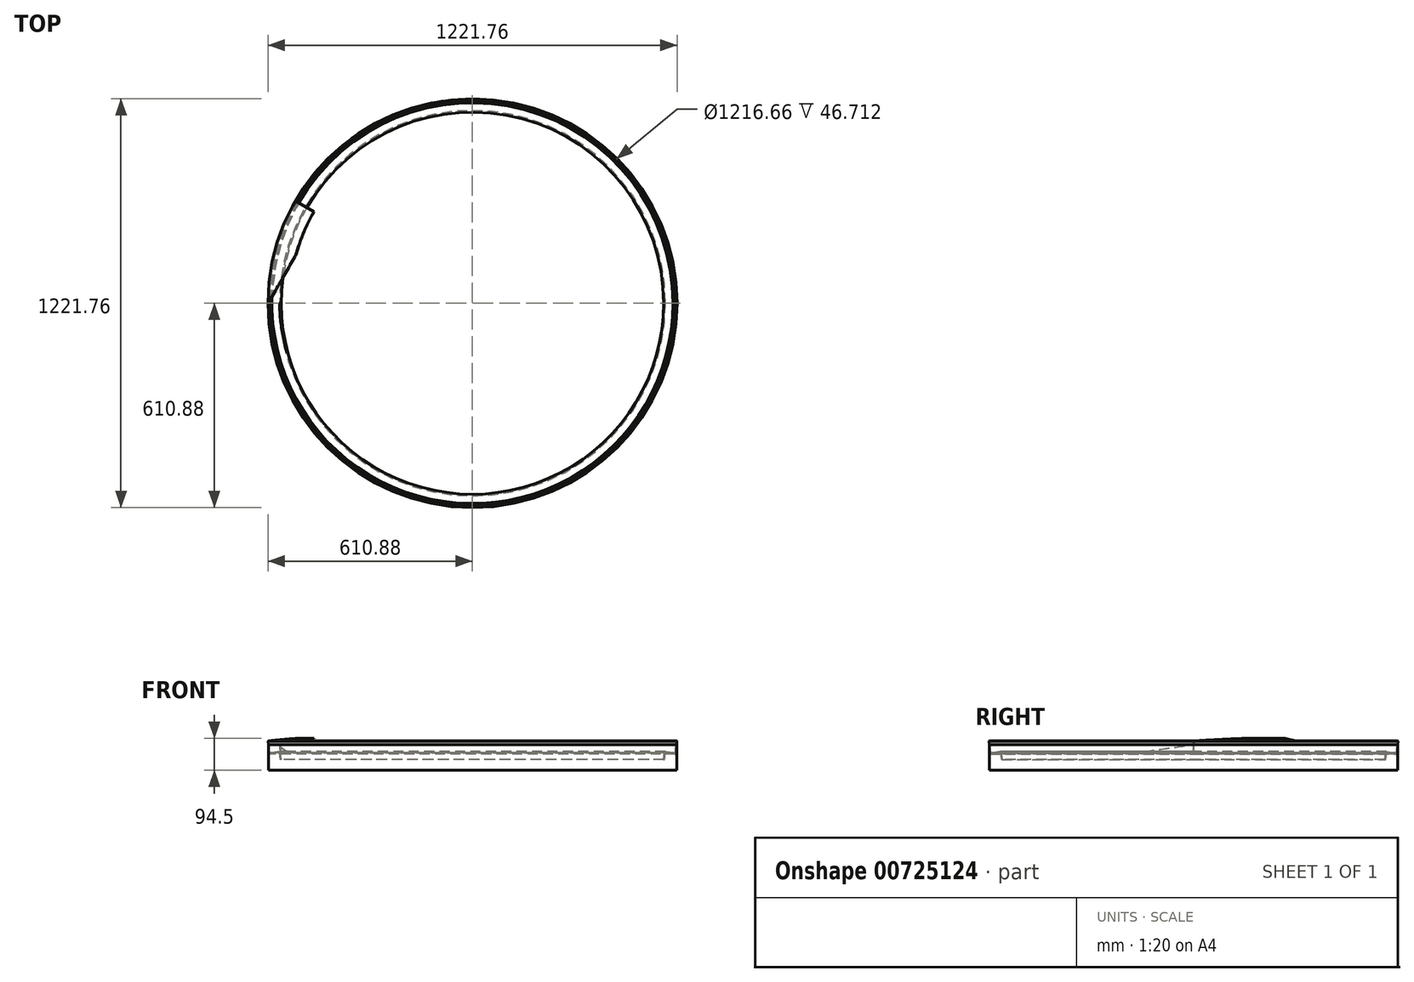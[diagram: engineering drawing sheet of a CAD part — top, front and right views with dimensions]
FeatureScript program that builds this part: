
annotation { "Feature Type Name" : "Feature", "Feature Type Description" : "" }
export const myFeature = defineFeature(function(context is Context, id is Id, definition is map)
    precondition{}
    {
        {
            var Q0;
            Q0=qCreatedBy(makeId("Front.planeOp"),FACE);
            var sketch = newSketch(context, id + "F0", { "sketchPlane" : qUnion([Q0])});
            skLineSegment(sketch, "E0.left", {"start": v(-609.6, -3.12) * mm, "end": v(-609.6, -53.92) * mm});
            skPoint(sketch, "E1.orphan", {"position": v(-609.6, 0) * mm});
            skLineSegment(sketch, "E2", {"start": v(-609.6, -3.12) * mm, "end": v(-609.6, 22.28) * mm});
            skLineSegment(sketch, "E3", {"start": v(-609.6, -53.92) * mm, "end": v(0, -53.92) * mm});
            skLineSegment(sketch, "E4", {"start": v(-608.33, -52.65) * mm, "end": v(-608.33, -5.94) * mm});
            skLineSegment(sketch, "E5", {"start": v(-608.33, -52.65) * mm, "end": v(0, -52.65) * mm});
            skLineSegment(sketch, "E6", {"start": v(0, -53.92) * mm, "end": v(0, -52.65) * mm});
            skLineSegment(sketch, "E7", {"start": v(-585.11, 0.11) * mm, "end": v(-573.8, 1.5) * mm});
            skLineSegment(sketch, "E8", {"start": v(-573.8, 1.5) * mm, "end": v(-573.4, -1.65) * mm});
            skLineSegment(sketch, "E9", {"start": v(-598.75, -1.56) * mm, "end": v(-585.11, 0.11) * mm});
            skLineSegment(sketch, "E10", {"start": v(-602.53, -2.03) * mm, "end": v(-605.3, -2.37) * mm});
            skLineSegment(sketch, "E11", {"start": v(-302.36, 34.83) * mm, "end": v(-302.2, 33.57) * mm});
            skLineSegment(sketch, "E12", {"start": v(-302.2, 33.57) * mm, "end": v(-298.43, 34.03) * mm});
            skLineSegment(sketch, "E13", {"start": v(-298.43, 34.03) * mm, "end": v(-298.58, 35.3) * mm});
            skLineSegment(sketch, "E14", {"start": v(-575.96, -1.96) * mm, "end": v(-608.33, -5.94) * mm});
            skLineSegment(sketch, "E15", {"start": v(-608.33, 22.28) * mm, "end": v(-605.3, -2.37) * mm});
            skLineSegment(sketch, "E16", {"start": v(-609.45, 31.42) * mm, "end": v(-546.42, 39.15) * mm});
            skLineSegment(sketch, "E17", {"start": v(-608.33, 22.28) * mm, "end": v(-609.45, 31.42) * mm});
            skLineSegment(sketch, "E18", {"start": v(-609.6, 22.28) * mm, "end": v(-610.72, 31.42) * mm});
            skLineSegment(sketch, "E19", {"start": v(-610.72, 31.42) * mm, "end": v(-610.88, 32.69) * mm});
            skLineSegment(sketch, "E20", {"start": v(-610.88, 32.69) * mm, "end": v(-546.6, 40.58) * mm});
            skLineSegment(sketch, "E21", {"start": v(-546.42, 39.15) * mm, "end": v(-546.6, 40.58) * mm});
            skLineSegment(sketch, "E22", {"start": v(-602.53, -2.03) * mm, "end": v(-602.38, -3.29) * mm});
            skLineSegment(sketch, "E23", {"start": v(-602.38, -3.29) * mm, "end": v(-598.6, -2.82) * mm});
            skLineSegment(sketch, "E24", {"start": v(-598.75, -1.56) * mm, "end": v(-598.6, -2.82) * mm});
            skLineSegment(sketch, "E25", {"start": v(-573.4, -1.65) * mm, "end": v(-570.85, -22.45) * mm});
            skLineSegment(sketch, "E26", {"start": v(-570.85, -22.45) * mm, "end": v(-573.4, -22.76) * mm});
            skLineSegment(sketch, "E27", {"start": v(-573.4, -22.76) * mm, "end": v(-575.96, -1.96) * mm});
            skLineSegment(sketch, "E28", {"start": v(-609.45, 31.42) * mm, "end": v(-609.63, 32.84) * mm});
            skLineSegment(sketch, "E29", {"start": v(-573.8, 1.5) * mm, "end": v(-576.27, 21.7) * mm});
            skLineSegment(sketch, "E30", {"start": v(-576.27, 21.7) * mm, "end": v(-574.79, 21.88) * mm});
            skLineSegment(sketch, "E31", {"start": v(-574.79, 21.88) * mm, "end": v(-572.28, 1.5) * mm});
            skLineSegment(sketch, "E32", {"start": v(-572.28, 1.5) * mm, "end": v(-573.8, 1.5) * mm});
            skSolve(sketch);
        }
        {
            var Q0;
            Q0=qCreatedBy(makeId("Front.planeOp"),FACE);
            var sketch = newSketch(context, id + "F1", { "sketchPlane" : qUnion([Q0])});
            skLineSegment(sketch, "E33", {"start": v(0, 40.5) * mm, "end": v(0, -62.38) * mm});
            skSolve(sketch);
        }
        {
            var Q0;
            Q0=makeQuery(id+"F0.imprint","IMPRINT",FACE,{"disambiguationData":[TD([[makeQuery(id+"F0.imprint","IMPRINT",EDGE,{"derivedFrom":sQuery(id+"F0.wireOp",EDGE,"E0.left")}),1.0]])]});
            var Q1;
            Q1=sQuery(id+"F1.wireOp",EDGE,"E33");
            revolve(context, id + "F2", {"surfaceOperationType" : NewSurfaceOperationType.NEW, "entities" : qUnion([Q0]), "axis" : qUnion([Q1]), "revolveType" : RevolveType.FULL});
        }
        {
            var Q0;
            Q0=makeQuery(id+"F2.opRevolve","SWEPT_FACE",FACE,{"disambiguationData":[OSD([sQuery(id+"F0.wireOp",EDGE,"E5")])]});
            var sketch = newSketch(context, id + "F3", { "sketchPlane" : qUnion([Q0])});
            skLineSegment(sketch, "E34", {"start": v(-608.33, 0) * mm, "end": v(-564.56, 113.43) * mm});
            skLineSegment(sketch, "E35", {"start": v(-564.56, 113.43) * mm, "end": v(-564.56, -4.64) * mm});
            skLineSegment(sketch, "E36", {"start": v(-564.56, -4.64) * mm, "end": v(-608.33, 0) * mm});
            skSolve(sketch);
        }
        {
            var Q0;
            Q0=makeQuery(id+"F0.imprint","IMPRINT",FACE,{"disambiguationData":[TD([[makeQuery(id+"F0.imprint","IMPRINT",EDGE,{"derivedFrom":sQuery(id+"F0.wireOp",EDGE,"E16")}),1.0]])]});
            var Q1;
            Q1=sQuery(id+"F1.wireOp",EDGE,"E33");
            revolve(context, id + "F4", {"operationType" : NewBodyOperationType.ADD, "surfaceOperationType" : NewSurfaceOperationType.NEW, "entities" : qUnion([Q0]), "axis" : qUnion([Q1]), "revolveType" : RevolveType.ONE_DIRECTION, "angle" : 30 * degree});
        }
        {
            var Q0;
            Q0=makeQuery(id+"F2.opRevolve","SWEPT_EDGE",EDGE,{"disambiguationData":[OSD([sQuery(id+"F0.wireOp",EDGE,"E7"),sQuery(id+"F0.wireOp",EDGE,"E8")])]});
            fillet(context, id + "F5", {"entities" : qUnion([Q0]), "radius" : 2.54 * mm, "tangentPropagation" : true, "allowEdgeOverflow" : false});
        }
        {
            var Q0;
            Q0=makeQuery(id+"F3.imprint","IMPRINT",FACE,{"disambiguationData":[TD([[makeQuery(id+"F3.imprint","IMPRINT",EDGE,{"derivedFrom":sQuery(id+"F3.wireOp",EDGE,"E34")}),-1.0]])]});
            cPlane(context, id + "F6", {"entities" : qUnion([Q0]), "cplaneType" : CPlaneType.OFFSET, "offset" : 76.2 * mm, "width" : 152.4 * mm, "height" : 152.4 * mm});
        }
        {
            var Q0;
            Q0=qCreatedBy(id+"F6.planeOp",FACE);
            var sketch = newSketch(context, id + "F7", { "sketchPlane" : qUnion([Q0])});
            skLineSegment(sketch, "E37", {"start": v(-609.34, 0) * mm, "end": v(-523.1, 151.67) * mm});
            skLineSegment(sketch, "E38", {"start": v(-523.1, 151.67) * mm, "end": v(-542.67, -7.21) * mm});
            skLineSegment(sketch, "E39", {"start": v(-542.67, -7.21) * mm, "end": v(-609.34, 0) * mm});
            skSolve(sketch);
        }
        {
            var Q0;
            Q0=makeQuery(id+"F7.imprint","IMPRINT",FACE,{"disambiguationData":[TD([[makeQuery(id+"F7.imprint","IMPRINT",EDGE,{"derivedFrom":sQuery(id+"F7.wireOp",EDGE,"E37")}),-1.0]])]});
            extrude(context, id + "F8", {"entities" : qUnion([Q0]), "operationType" : NewBodyOperationType.REMOVE, "depth" : 25.4 * mm, "offsetDistance" : 25.4 * mm});
        }
        {
            var Q0;
            Q0=makeQuery(id+"F0.imprint","IMPRINT",FACE,{"disambiguationData":[TD([[makeQuery(id+"F0.imprint","IMPRINT",EDGE,{"derivedFrom":sQuery(id+"F0.wireOp",EDGE,"E29")}),-1.0]])]});
            var Q1;
            Q1=sQuery(id+"F1.wireOp",EDGE,"E33");
            revolve(context, id + "F9", {"surfaceOperationType" : NewSurfaceOperationType.NEW, "entities" : qUnion([Q0]), "axis" : qUnion([Q1]), "revolveType" : RevolveType.ONE_DIRECTION, "oppositeDirection" : true, "angle" : 15 * degree});
        }
        {
            var Q0;
            Q0=qCreatedBy(makeId("Right.planeOp"),FACE);
            var sketch = newSketch(context, id + "F10", { "sketchPlane" : qUnion([Q0])});
            skLineSegment(sketch, "E40", {"start": v(-148.51, 1.54) * mm, "end": v(0.47, 21.95) * mm});
            skLineSegment(sketch, "E41", {"start": v(0.47, 21.95) * mm, "end": v(-149.5, 21.95) * mm});
            skLineSegment(sketch, "E42", {"start": v(-149.5, 21.95) * mm, "end": v(-148.51, 1.54) * mm});
            skSolve(sketch);
        }
        {
            var Q0;
            Q0=makeQuery(id+"F10.imprint","IMPRINT",FACE,{"disambiguationData":[TD([[makeQuery(id+"F10.imprint","IMPRINT",EDGE,{"derivedFrom":sQuery(id+"F10.wireOp",EDGE,"E40")}),1.0]])]});
            extrude(context, id + "F11", {"entities" : qUnion([Q0]), "operationType" : NewBodyOperationType.REMOVE, "oppositeDirection" : true, "depth" : 584.2 * mm, "offsetDistance" : 25.4 * mm});
        }
    });
